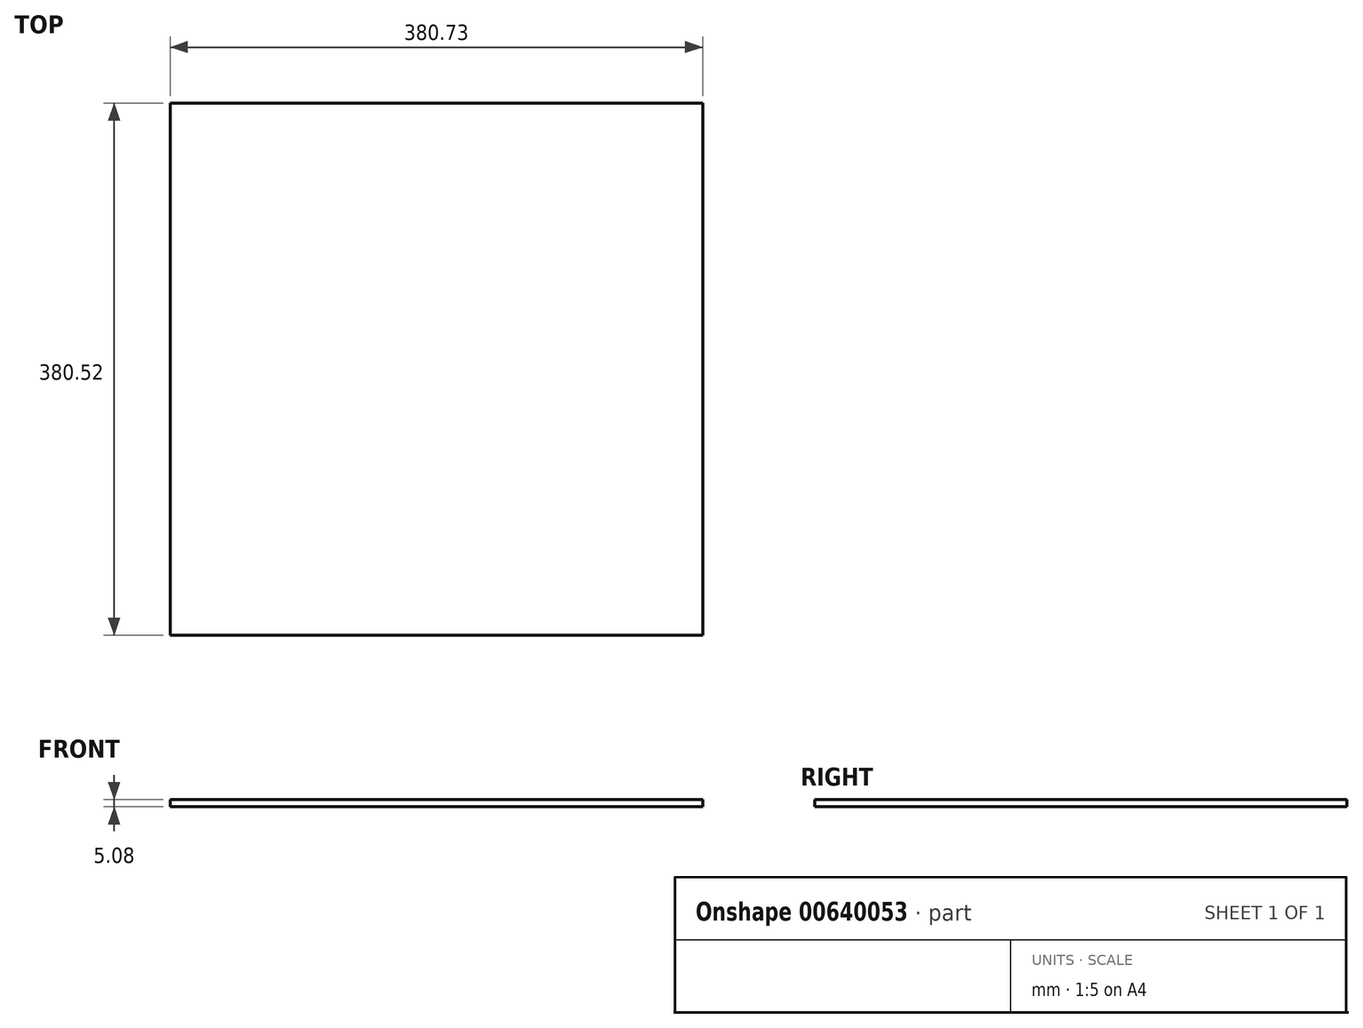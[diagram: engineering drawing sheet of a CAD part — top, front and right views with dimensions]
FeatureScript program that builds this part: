
annotation { "Feature Type Name" : "Feature", "Feature Type Description" : "" }
export const myFeature = defineFeature(function(context is Context, id is Id, definition is map)
    precondition{}
    {
        {
            var Q0;
            Q0=qCreatedBy(makeId("Top.planeOp"),FACE);
            var sketch = newSketch(context, id + "F0", { "sketchPlane" : qUnion([Q0])});
            skLineSegment(sketch, "E0", {"start": v(0, 0) * mm, "end": v(-75.93, 0) * mm});
            skLineSegment(sketch, "E1", {"start": v(-75.93, 0) * mm, "end": v(-75.93, -75.72) * mm});
            skLineSegment(sketch, "E2", {"start": v(-75.93, -75.72) * mm, "end": v(0, -75.72) * mm});
            skLineSegment(sketch, "E3", {"start": v(0, -75.72) * mm, "end": v(0, 0) * mm});
            skSolve(sketch);
        }
        {
            var Q0;
            Q0=makeQuery(id+"F0.imprint","IMPRINT",FACE,{"disambiguationData":[TD([[makeQuery(id+"F0.imprint","IMPRINT",EDGE,{"derivedFrom":sQuery(id+"F0.wireOp",EDGE,"E0")}),1.0]])]});
            extrude(context, id + "F1", {"entities" : qUnion([Q0]), "depth" : 5.08 * mm, "offsetDistance" : 25.4 * mm});
        }
        {
            var Q0;
            Q0=makeQuery(id+"F1.opExtrude","SWEPT_FACE",FACE,{"disambiguationData":[OSD([sQuery(id+"F0.wireOp",EDGE,"E2")])]});
            extrude(context, id + "F2", {"entities" : qUnion([Q0]), "operationType" : NewBodyOperationType.ADD, "depth" : 304.8 * mm, "offsetDistance" : 25.4 * mm});
        }
        {
            var Q0;
            {var subQ0=sQuery(id+"F0.wireOp",EDGE,"E1");Q0=makeQuery(id+"F2.boolean.opBoolean","MERGE",FACE,{"derivedFrom":[makeQuery(id+"F1.opExtrude","SWEPT_FACE",FACE,{"disambiguationData":[OSD([subQ0])]}),makeQuery(id+"F2.opExtrude","SWEPT_FACE",FACE,{"disambiguationData":[OSD([subQ0,sQuery(id+"F0.wireOp",EDGE,"E2")])]})]});}
            extrude(context, id + "F3", {"entities" : qUnion([Q0]), "operationType" : NewBodyOperationType.ADD, "depth" : 304.8 * mm, "offsetDistance" : 25.4 * mm});
        }
    });
